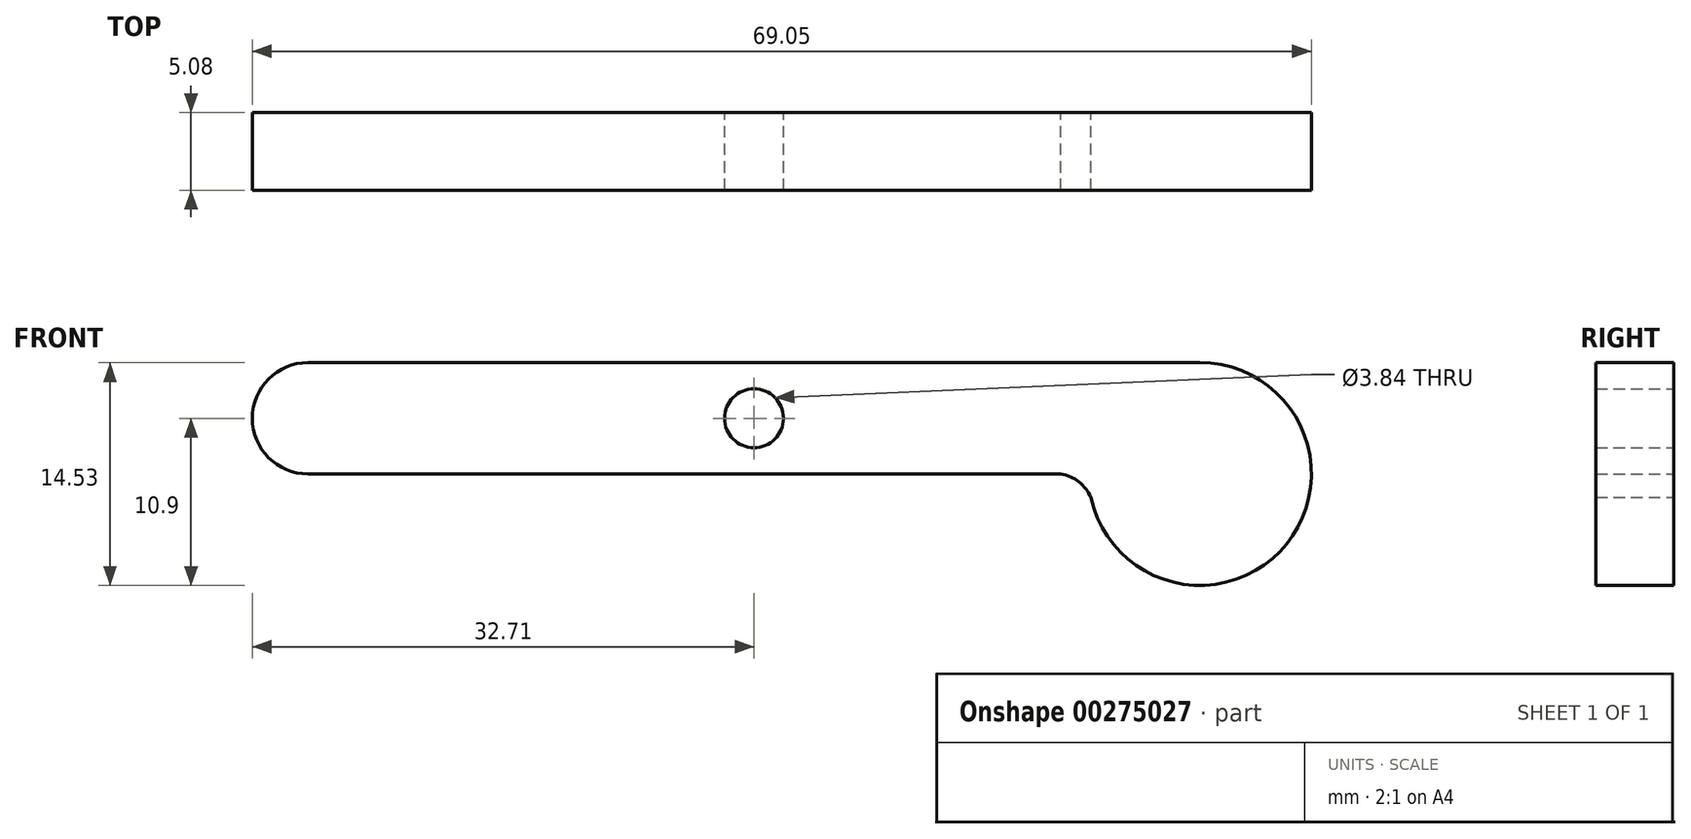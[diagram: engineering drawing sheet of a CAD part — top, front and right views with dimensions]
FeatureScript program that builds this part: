
annotation { "Feature Type Name" : "Feature", "Feature Type Description" : "" }
export const myFeature = defineFeature(function(context is Context, id is Id, definition is map)
    precondition{}
    {
        {
            var Q0;
            Q0=qCreatedBy(makeId("Front.planeOp"),FACE);
            var sketch = newSketch(context, id + "F0", { "sketchPlane" : qUnion([Q0])});
            skLineSegment(sketch, "E0.bottom", {"start": v(20, -3.63) * mm, "end": v(-29.07, -3.63) * mm});
            skLineSegment(sketch, "E0.top", {"start": v(29.07, 3.63) * mm, "end": v(-29.07, 3.63) * mm});
            skPoint(sketch, "E0.middle", {"position": v(0, 0) * mm});
            skArc(sketch, "E1", {"start": v(-29.07, 3.63) * mm, "mid": v(-32.7, 0) * mm, "end": v(-29.07, -3.63) * mm});
            skCircle(sketch, "E2", {"center": v(0, 0) * mm, "radius": 1.92 * mm});
            skArc(sketch, "E3", {"start": v(21.97, -5.16) * mm, "mid": v(34.73, -8.2) * mm, "end": v(29.07, 3.63) * mm});
            skArc(sketch, "E4", {"start": v(21.97, -5.16) * mm, "mid": v(21.18, -4.15) * mm, "end": v(20, -3.63) * mm});
            skSolve(sketch);
        }
        {
            var Q0;
            Q0 = qSketchRegion(id + "F0", true);
            extrude(context, id + "F1", {"entities" : qUnion([Q0]), "depth" : 5.08 * mm});
        }
    });
